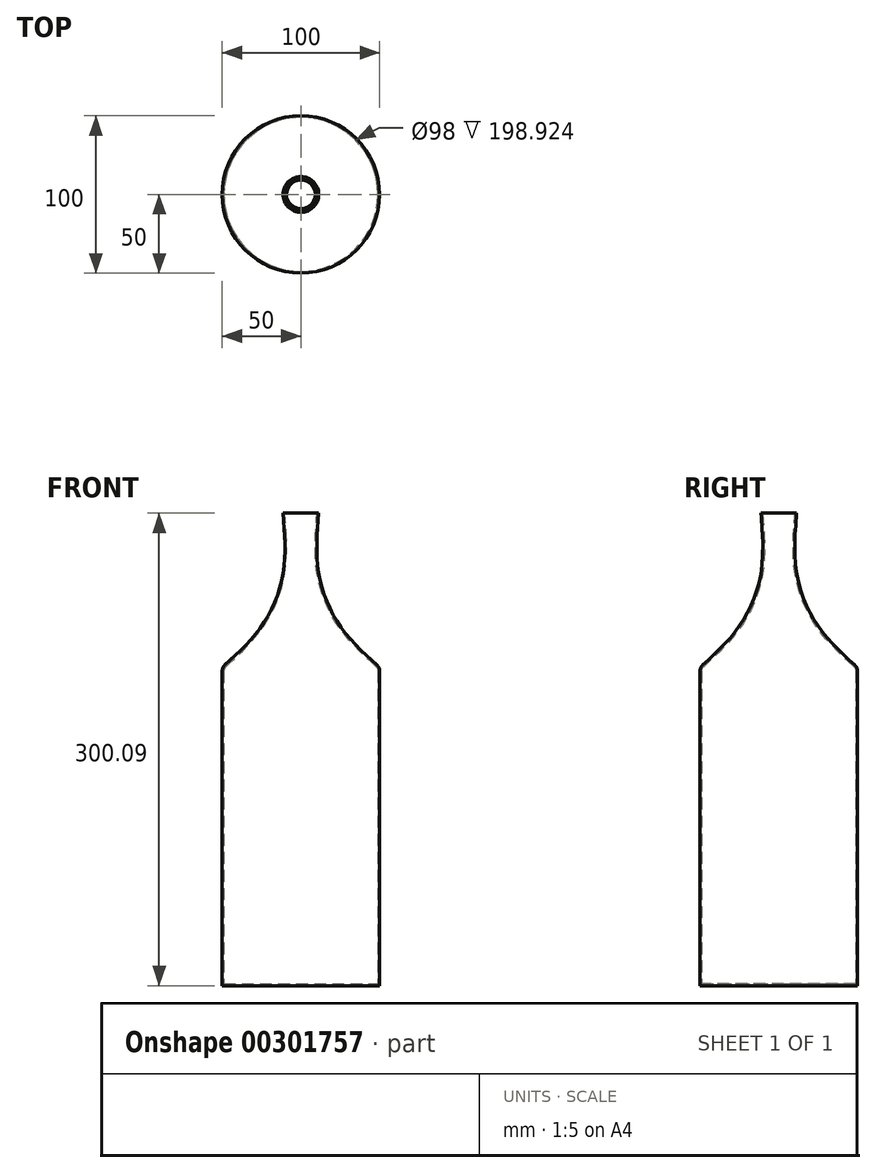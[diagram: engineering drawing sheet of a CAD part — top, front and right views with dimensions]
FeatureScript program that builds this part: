
annotation { "Feature Type Name" : "Feature", "Feature Type Description" : "" }
export const myFeature = defineFeature(function(context is Context, id is Id, definition is map)
    precondition{}
    {
        {
            var Q0;
            Q0=qCreatedBy(makeId("Right.planeOp"),FACE);
            var sketch = newSketch(context, id + "F0", { "sketchPlane" : qUnion([Q0])});
            skLineSegment(sketch, "E0", {"start": v(0, 0) * mm, "end": v(0, 300) * mm});
            skLineSegment(sketch, "E1", {"start": v(0, 0) * mm, "end": v(-50, 0) * mm});
            skLineSegment(sketch, "E2", {"start": v(-50, 0) * mm, "end": v(-50, 202.15) * mm});
            skLineSegment(sketch, "E3", {"start": v(0, 300) * mm, "end": v(-11.35, 300.09) * mm});
            skFitSpline(sketch, "E4", {"points": [v(-11.35, 300.09) * mm, v(-11.35, 261.9) * mm, v(-25.4, 227.84) * mm, v(-50, 202.15) * mm], "startDerivative": vector(9.1, -113.74) * mm, "endDerivative": vector(-81.09, -72.86) * mm});
            skSolve(sketch);
        }
        {
            var Q0;
            Q0=makeQuery(id+"F0.imprint","IMPRINT",FACE,{"disambiguationData":[TD([[makeQuery(id+"F0.imprint","IMPRINT",EDGE,{"derivedFrom":sQuery(id+"F0.wireOp",EDGE,"E0")}),1.0]])]});
            var Q1;
            Q1=sQuery(id+"F0.wireOp",EDGE,"E0");
            revolve(context, id + "F1", {"entities" : qUnion([Q0]), "axis" : qUnion([Q1]), "revolveType" : RevolveType.FULL});
        }
        {
            var Q0;
            Q0=makeQuery(id+"F1.opRevolve","SWEPT_EDGE",EDGE,{"disambiguationData":[OSD([sQuery(id+"F0.wireOp",EDGE,"E2"),sQuery(id+"F0.wireOp",EDGE,"E4")])]});
            fillet(context, id + "F2", {"entities" : qUnion([Q0]), "radius" : 5 * mm, "tangentPropagation" : true, "allowEdgeOverflow" : false});
        }
        {
            var Q0;
            Q0=makeQuery(id+"F1.opRevolve","SWEPT_FACE",FACE,{"disambiguationData":[OSD([sQuery(id+"F0.wireOp",EDGE,"E3")])]});
            shell(context, id + "F3", {"entities" : qUnion([Q0]), "thickness" : 1 * mm});
        }
    });
